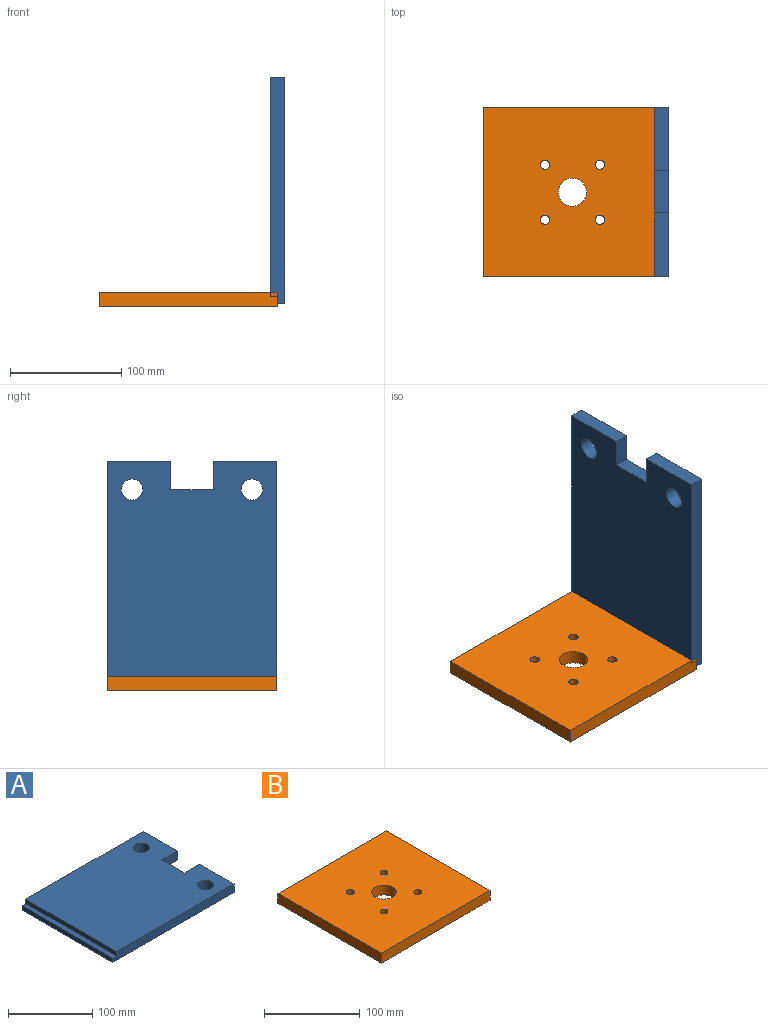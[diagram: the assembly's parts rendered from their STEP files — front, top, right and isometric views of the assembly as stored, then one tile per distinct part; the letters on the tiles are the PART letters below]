
ASSEMBLY  parts=2 mates=1
PART A: 14 faces, bbox 203.2x152.4x12.7 mm
  f0: plane 152.4x6.35mm, normal (-1,0,0), area 967.7mm2, adj f2,f7,f11,f13
  f1: plane 196.85x152.4mm, normal (0,0,1), area 28449.4mm2, adj f2,f3,f4,f5,f6,f7,f8,f9
  f2: plane 203.2x12.7mm, normal (0,1,0), area 2540.3mm2, adj f0,f1,f6,f11,f12,f13
  f3: plane 25.74x12.7mm, normal (0,1,0), area 326.8mm2, adj f1,f4,f9,f11
  f4: plane 38.1x12.7mm, normal (1,0,0), area 483.9mm2, adj f1,f3,f5,f11
  f5: plane 25.74x12.7mm, normal (0,-1,0), area 326.8mm2, adj f1,f4,f6,f11
  f6: plane 57.15x12.7mm, normal (1,0,0), area 725.8mm2, adj f1,f2,f5,f11
  f7: plane 203.2x12.7mm, normal (0,-1,0), area 2540.3mm2, adj f0,f1,f9,f11,f12,f13
  f8: cylinder r=9.53mm len=19.05mm, axis (0,0,-1), area 760.1mm2, adj f1,f11
  f9: plane 57.15x12.7mm, normal (1,0,0), area 725.8mm2, adj f1,f3,f7,f11
  f10: cylinder r=9.53mm len=19.05mm, axis (0,0,-1), area 760.1mm2, adj f1,f11
  f11: plane 203.2x152.4mm, normal (0,0,-1), area 29417.1mm2, adj f0,f2,f3,f4,f5,f6,f7,f8
  f12: plane 152.4x6.35mm, normal (-1,0,0), area 967.7mm2, adj f1,f2,f7,f13
  f13: plane 152.4x6.35mm, normal (0,0,1), area 967.7mm2, adj f0,f2,f7,f12
PART B: 11 faces, bbox 160.3x152.4x12.7 mm
  f0: plane 160.34x12.7mm, normal (0,1,0), area 2036.3mm2, adj f1,f3,f9,f10
  f1: plane 152.4x12.7mm, normal (-1,0,0), area 1935.5mm2, adj f0,f2,f9,f10
  f2: plane 160.34x12.7mm, normal (0,-1,0), area 2036.3mm2, adj f1,f3,f9,f10
  f3: plane 152.4x12.7mm, normal (1,0,0), area 1935.5mm2, adj f0,f2,f9,f10
  f4: cylinder r=12.7mm len=25.4mm, axis (0,0,-1), area 1013.4mm2, adj f9,f10
  f5: cylinder r=4.17mm len=12.7mm, axis (0,0,-1), area 332.4mm2, adj f9,f10
  f6: cylinder r=4.17mm len=12.7mm, axis (0,0,-1), area 332.4mm2, adj f9,f10
  f7: cylinder r=4.17mm len=12.7mm, axis (0,0,-1), area 332.4mm2, adj f9,f10
  f8: cylinder r=4.17mm len=12.7mm, axis (0,0,-1), area 332.4mm2, adj f9,f10
  f9: plane 160.34x152.4mm, normal (0,0,1), area 23710.7mm2, adj f0,f1,f2,f3,f4,f5,f6,f7
  f10: plane 160.34x152.4mm, normal (0,0,-1), area 23710.7mm2, adj f0,f1,f2,f3,f4,f5,f6,f7
PLACE A rot(axis=(0,-1,0),90deg) t=(123.28,20.7,196.71)mm
PLACE B t=(36.76,20.7,91.94)mm
MATE fastened A.f13 <-> B.f3  axis (-1,0,0) through (116.93,20.7,98.29)mm
